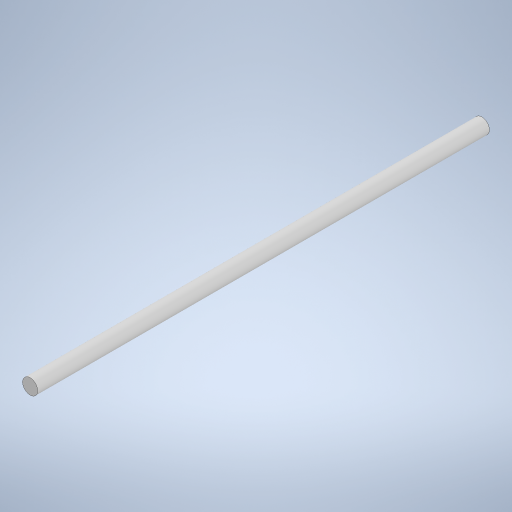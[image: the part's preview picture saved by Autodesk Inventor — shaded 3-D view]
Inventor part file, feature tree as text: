
AUTODESK INVENTOR PART (.ipt)
format: ipt  version: 2024 (Build 280153000, 153)  size: 231,936 bytes
history: native  units: mm
features: other x1, extrude x1, sketch x1
ambient origin geometry x8: Origin, YZ Plane, XZ Plane, XY Plane, X Axis, Y Axis, Z Axis, Center Point
bodies: Body1 (feature_tree)
feature tree (3):
  other  "솔리드1"
  extrude  "돌출1"  Depth=4.0mm
  sketch  "스케치1"
